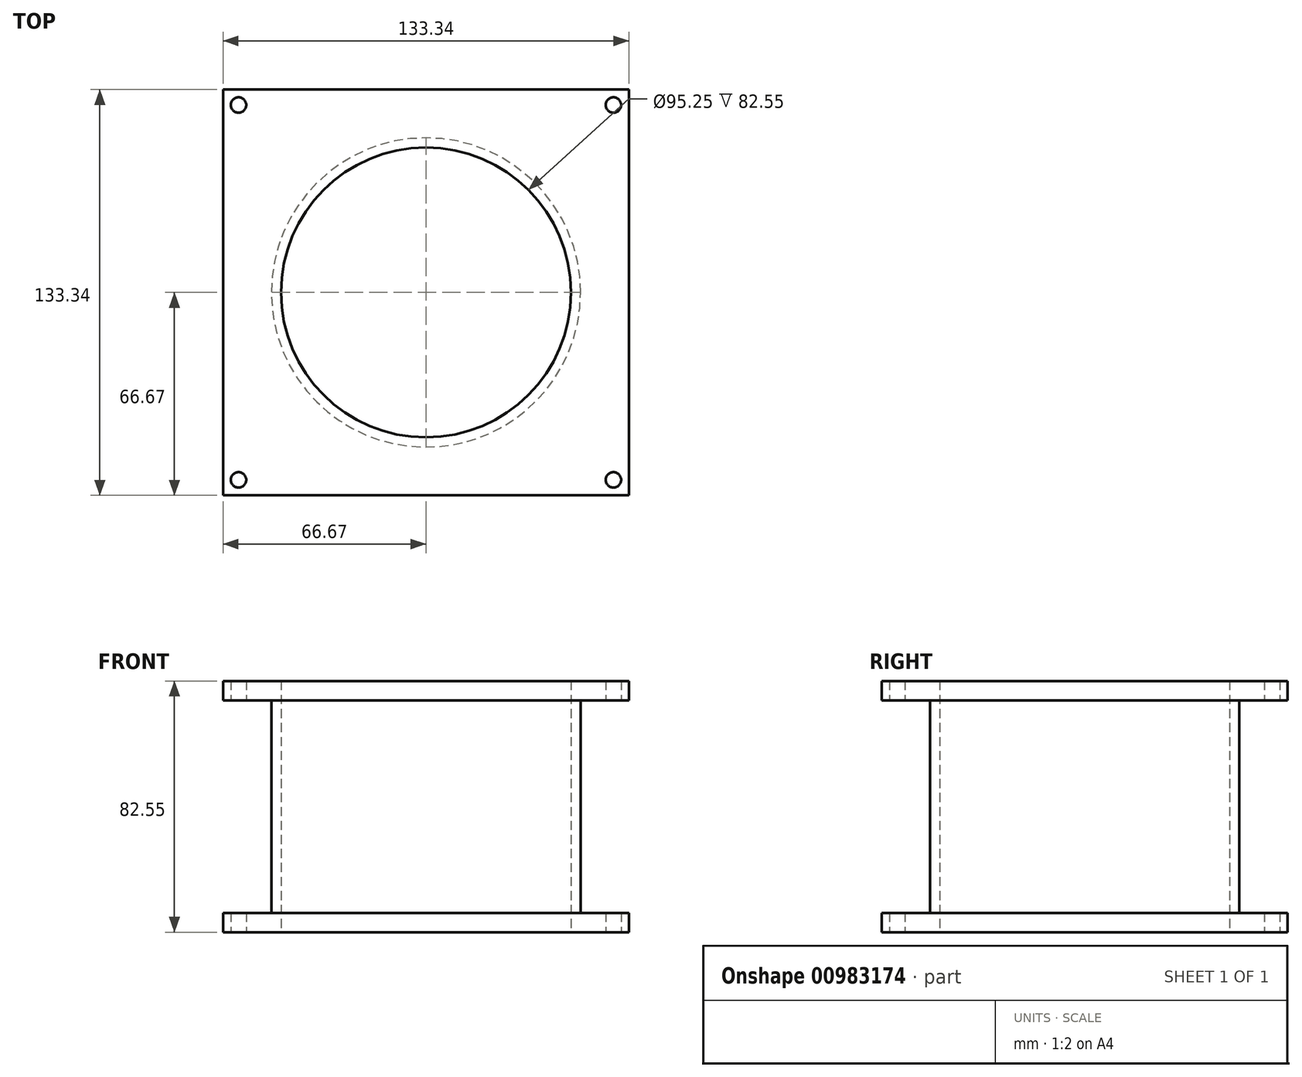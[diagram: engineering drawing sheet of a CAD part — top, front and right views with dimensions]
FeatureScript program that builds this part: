
annotation { "Feature Type Name" : "Feature", "Feature Type Description" : "" }
export const myFeature = defineFeature(function(context is Context, id is Id, definition is map)
    precondition{}
    {
        {
            var Q0;
            Q0=qCreatedBy(makeId("Top.planeOp"),FACE);
            var sketch = newSketch(context, id + "F0", { "sketchPlane" : qUnion([Q0])});
            skLineSegment(sketch, "E0.bottom", {"start": v(-66.67, 66.68) * mm, "end": v(66.68, 66.68) * mm});
            skLineSegment(sketch, "E0.top", {"start": v(-66.68, -66.68) * mm, "end": v(66.67, -66.68) * mm});
            skLineSegment(sketch, "E0.left", {"start": v(-66.67, 66.68) * mm, "end": v(-66.68, -66.67) * mm});
            skLineSegment(sketch, "E0.right", {"start": v(66.68, 66.68) * mm, "end": v(66.67, -66.67) * mm});
            skPoint(sketch, "E0.middle", {"position": v(0, 0) * mm});
            skCircle(sketch, "E1", {"center": v(-61.6, 61.6) * mm, "radius": 2.54 * mm});
            skCircle(sketch, "E2", {"center": v(61.6, 61.6) * mm, "radius": 2.54 * mm});
            skCircle(sketch, "E3", {"center": v(-61.6, -61.6) * mm, "radius": 2.54 * mm});
            skCircle(sketch, "E4", {"center": v(61.6, -61.6) * mm, "radius": 2.54 * mm});
            skCircle(sketch, "E5", {"center": v(0, 0) * mm, "radius": 50.8 * mm});
            skCircle(sketch, "E6", {"center": v(0, 0) * mm, "radius": 47.63 * mm});
            skSolve(sketch);
        }
        {
            var Q0;
            Q0=makeQuery(id+"F0.imprint","IMPRINT",FACE,{"disambiguationData":[TD([[makeQuery(id+"F0.imprint","IMPRINT",EDGE,{"derivedFrom":sQuery(id+"F0.wireOp",EDGE,"E5")}),1.0]])]});
            extrude(context, id + "F1", {"entities" : qUnion([Q0]), "depth" : 76.2 * mm, "offsetDistance" : 25.4 * mm});
        }
        {
            var Q0;
            Q0=qSketchRegion(id+"F0",true);
            extrude(context, id + "F2", {"entities" : qUnion([Q0]), "operationType" : NewBodyOperationType.ADD, "depth" : 6.35 * mm, "offsetDistance" : 25.4 * mm});
        }
        {
            var Q0;
            Q0=makeQuery(id+"F1.opExtrude","CAP_FACE",FACE,{"disambiguationData":[OSD([sQuery(id+"F0.wireOp",EDGE,"E5"),sQuery(id+"F0.wireOp",EDGE,"E6")])],"isStart":false});
            var sketch = newSketch(context, id + "F3", { "sketchPlane" : qUnion([Q0])});
            skLineSegment(sketch, "E7.bottom", {"start": v(66.68, -66.68) * mm, "end": v(-66.68, -66.68) * mm});
            skLineSegment(sketch, "E7.top", {"start": v(66.68, 66.68) * mm, "end": v(-66.68, 66.68) * mm});
            skLineSegment(sketch, "E7.left", {"start": v(66.68, -66.68) * mm, "end": v(66.68, 66.68) * mm});
            skLineSegment(sketch, "E7.right", {"start": v(-66.68, -66.68) * mm, "end": v(-66.68, 66.67) * mm});
            skPoint(sketch, "E7.middle", {"position": v(0, 0) * mm});
            skCircle(sketch, "E8", {"center": v(-61.6, -61.6) * mm, "radius": 2.54 * mm});
            skCircle(sketch, "E9", {"center": v(-61.6, 61.6) * mm, "radius": 2.54 * mm});
            skCircle(sketch, "E10", {"center": v(61.6, 61.6) * mm, "radius": 2.54 * mm});
            skCircle(sketch, "E11", {"center": v(61.6, -61.6) * mm, "radius": 2.54 * mm});
            skCircle(sketch, "E12", {"center": v(0, 0) * mm, "radius": 47.63 * mm});
            skCircle(sketch, "E13", {"center": v(0, 0) * mm, "radius": 50.8 * mm});
            skSolve(sketch);
        }
        {
            var Q0;
            Q0=makeQuery(id+"F3.imprint","IMPRINT",FACE,{"disambiguationData":[TD([[makeQuery(id+"F3.imprint","IMPRINT",EDGE,{"derivedFrom":sQuery(id+"F3.wireOp",EDGE,"E12")}),-1.0]])]});
            extrude(context, id + "F4", {"entities" : qUnion([Q0]), "operationType" : NewBodyOperationType.ADD, "depth" : 6.35 * mm, "offsetDistance" : 25.4 * mm});
        }
        {
            var Q0;
            Q0 = qSketchRegion(id + "F3", true);
            extrude(context, id + "F5", {"entities" : qUnion([Q0]), "operationType" : NewBodyOperationType.ADD, "depth" : 6.35 * mm, "offsetDistance" : 25.4 * mm});
        }
    });
